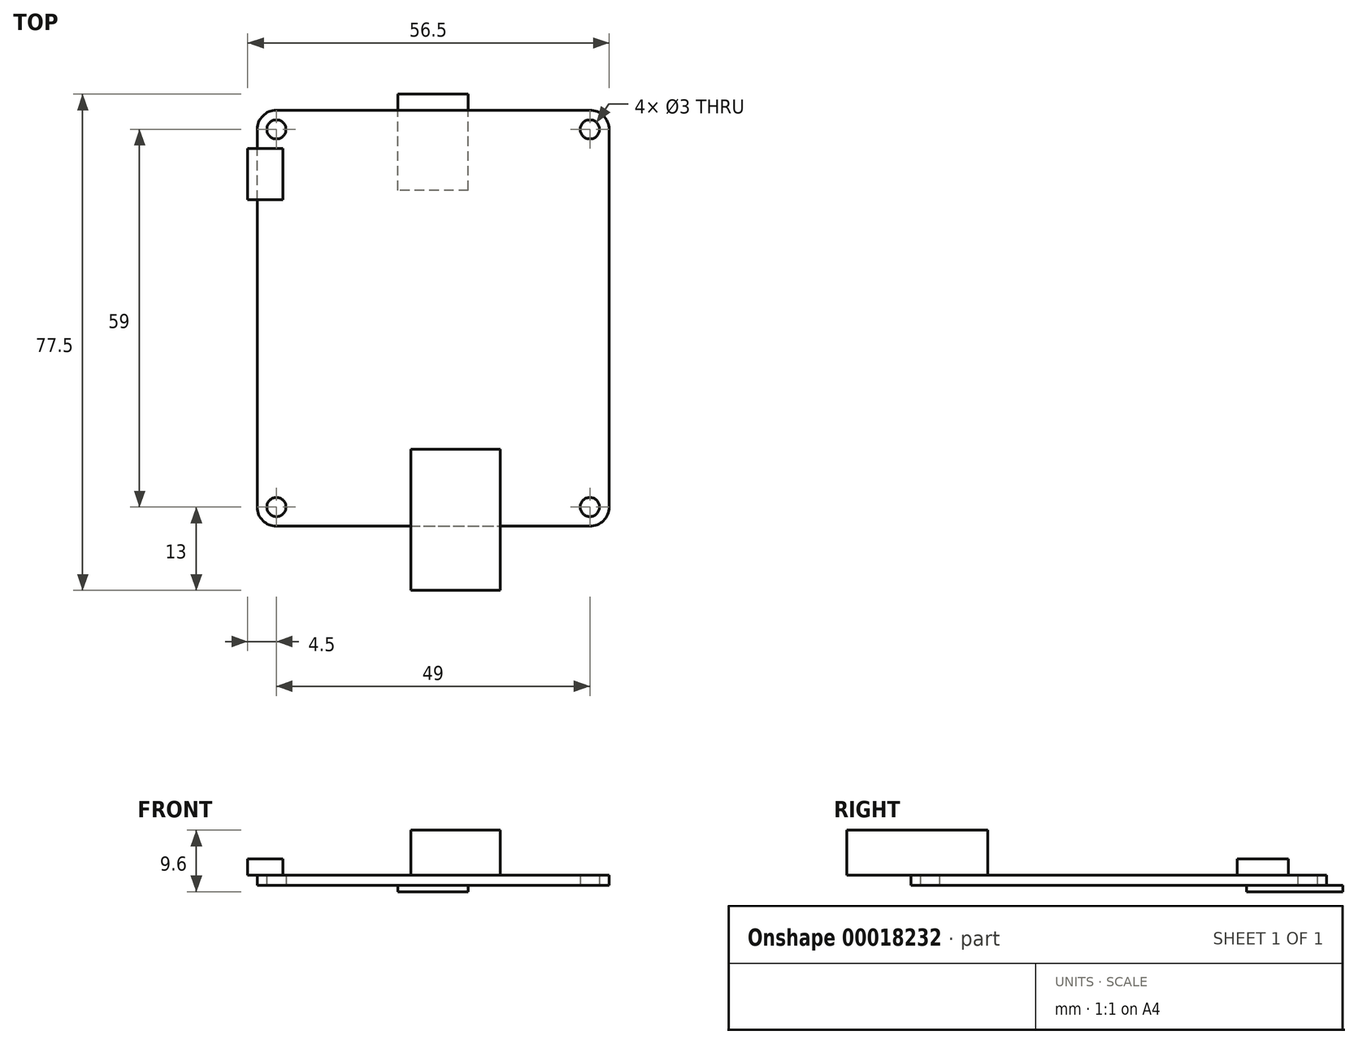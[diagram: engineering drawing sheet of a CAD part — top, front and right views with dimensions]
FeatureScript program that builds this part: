
annotation { "Feature Type Name" : "Feature", "Feature Type Description" : "" }
export const myFeature = defineFeature(function(context is Context, id is Id, definition is map)
    precondition{}
    {
        {
            var Q0;
            Q0=qCreatedBy(makeId("Top.planeOp"),FACE);
            var sketch = newSketch(context, id + "F0", { "sketchPlane" : qUnion([Q0])});
            skLineSegment(sketch, "E0.bottom", {"start": v(3, 0) * mm, "end": v(52, 0) * mm});
            skLineSegment(sketch, "E0.top", {"start": v(3, 65) * mm, "end": v(52, 65) * mm});
            skLineSegment(sketch, "E0.left", {"start": v(0, 3) * mm, "end": v(0, 62) * mm});
            skLineSegment(sketch, "E0.right", {"start": v(55, 3) * mm, "end": v(55, 62) * mm});
            skPoint(sketch, "E1.visualSharp", {"position": v(0, 0) * mm});
            skArc(sketch, "E1.filletArc", {"start": v(0, 3) * mm, "mid": v(0.88, 0.88) * mm, "end": v(3, 0) * mm});
            skPoint(sketch, "E2.visualSharp", {"position": v(0, 65) * mm});
            skArc(sketch, "E2.filletArc", {"start": v(3, 65) * mm, "mid": v(0.88, 64.12) * mm, "end": v(0, 62) * mm});
            skPoint(sketch, "E3.visualSharp", {"position": v(55, 65) * mm});
            skArc(sketch, "E3.filletArc", {"start": v(55, 62) * mm, "mid": v(54.12, 64.12) * mm, "end": v(52, 65) * mm});
            skPoint(sketch, "E4.visualSharp", {"position": v(55, 0) * mm});
            skArc(sketch, "E4.filletArc", {"start": v(52, 0) * mm, "mid": v(54.12, 0.88) * mm, "end": v(55, 3) * mm});
            skCircle(sketch, "E5", {"center": v(3, 3) * mm, "radius": 1.5 * mm});
            skCircle(sketch, "E6", {"center": v(52, 3) * mm, "radius": 1.5 * mm});
            skCircle(sketch, "E7", {"center": v(52, 62) * mm, "radius": 1.5 * mm});
            skCircle(sketch, "E8", {"center": v(3, 62) * mm, "radius": 1.5 * mm});
            skSolve(sketch);
        }
        {
            var Q0;
            Q0=makeQuery(id+"F0.imprint","IMPRINT",FACE,{"disambiguationData":[TD([[makeQuery(id+"F0.imprint","IMPRINT",EDGE,{"derivedFrom":sQuery(id+"F0.wireOp",EDGE,"E0.bottom")}),1.0]])]});
            extrude(context, id + "F1", {"entities" : qUnion([Q0]), "depth" : 1.6 * mm});
        }
        {
            var Q0;
            Q0=makeQuery(id+"F1.opExtrude","CAP_FACE",FACE,{"disambiguationData":[OSD([sQuery(id+"F0.wireOp",EDGE,"E0.bottom"),sQuery(id+"F0.wireOp",EDGE,"E0.top"),sQuery(id+"F0.wireOp",EDGE,"E0.left"),sQuery(id+"F0.wireOp",EDGE,"E0.right"),sQuery(id+"F0.wireOp",EDGE,"E1.filletArc"),sQuery(id+"F0.wireOp",EDGE,"E2.filletArc"),sQuery(id+"F0.wireOp",EDGE,"E3.filletArc"),sQuery(id+"F0.wireOp",EDGE,"E4.filletArc"),sQuery(id+"F0.wireOp",EDGE,"E5"),sQuery(id+"F0.wireOp",EDGE,"E6"),sQuery(id+"F0.wireOp",EDGE,"E7"),sQuery(id+"F0.wireOp",EDGE,"E8")])],"isStart":false});
            var sketch = newSketch(context, id + "F2", { "sketchPlane" : qUnion([Q0])});
            skLineSegment(sketch, "E9.bottom", {"start": v(24, 12) * mm, "end": v(38, 12) * mm});
            skLineSegment(sketch, "E9.top", {"start": v(24, -10) * mm, "end": v(38, -10) * mm});
            skLineSegment(sketch, "E9.left", {"start": v(24, 12) * mm, "end": v(24, -10) * mm});
            skLineSegment(sketch, "E9.right", {"start": v(38, 12) * mm, "end": v(38, -10) * mm});
            skLineSegment(sketch, "E10.bottom", {"start": v(4, 59) * mm, "end": v(-1.5, 59) * mm});
            skLineSegment(sketch, "E10.top", {"start": v(4, 51) * mm, "end": v(-1.5, 51) * mm});
            skLineSegment(sketch, "E10.left", {"start": v(4, 59) * mm, "end": v(4, 51) * mm});
            skLineSegment(sketch, "E10.right", {"start": v(-1.5, 59) * mm, "end": v(-1.5, 51) * mm});
            skSolve(sketch);
        }
        {
            var Q0;
            {var subQ3=sQuery(id+"F2.wireOp",EDGE,"E9.bottom");Q0=makeQuery(id+"F2.imprint","IMPRINT",FACE,{"disambiguationData":[TD([[makeQuery(id+"F2.imprint","IMPRINT",EDGE,{"derivedFrom":subQ3}),-1.0]])]});}
            var Q1;
            {var subQ5=sQuery(id+"F2.wireOp",EDGE,"E9.top");Q1=makeQuery(id+"F2.imprint","IMPRINT",FACE,{"disambiguationData":[TD([[makeQuery(id+"F2.imprint","IMPRINT",EDGE,{"derivedFrom":subQ5}),1.0]])]});}
            extrude(context, id + "F3", {"entities" : qUnion([Q0, Q1]), "operationType" : NewBodyOperationType.ADD, "depth" : 7 * mm});
        }
        {
            var Q0;
            {var subQ5=sQuery(id+"F2.wireOp",EDGE,"E10.left");Q0=makeQuery(id+"F2.imprint","IMPRINT",FACE,{"disambiguationData":[TD([[makeQuery(id+"F2.imprint","IMPRINT",EDGE,{"derivedFrom":subQ5}),-1.0]])]});}
            var Q1;
            {var subQ5=sQuery(id+"F2.wireOp",EDGE,"E10.right");Q1=makeQuery(id+"F2.imprint","IMPRINT",FACE,{"disambiguationData":[TD([[makeQuery(id+"F2.imprint","IMPRINT",EDGE,{"derivedFrom":subQ5}),1.0]])]});}
            extrude(context, id + "F4", {"entities" : qUnion([Q0, Q1]), "operationType" : NewBodyOperationType.ADD, "depth" : 2.5 * mm});
        }
        {
            var Q0;
            Q0=makeQuery(id+"F1.opExtrude","CAP_FACE",FACE,{"disambiguationData":[OSD([sQuery(id+"F0.wireOp",EDGE,"E0.bottom"),sQuery(id+"F0.wireOp",EDGE,"E0.top"),sQuery(id+"F0.wireOp",EDGE,"E0.left"),sQuery(id+"F0.wireOp",EDGE,"E0.right"),sQuery(id+"F0.wireOp",EDGE,"E1.filletArc"),sQuery(id+"F0.wireOp",EDGE,"E2.filletArc"),sQuery(id+"F0.wireOp",EDGE,"E3.filletArc"),sQuery(id+"F0.wireOp",EDGE,"E4.filletArc"),sQuery(id+"F0.wireOp",EDGE,"E5"),sQuery(id+"F0.wireOp",EDGE,"E6"),sQuery(id+"F0.wireOp",EDGE,"E7"),sQuery(id+"F0.wireOp",EDGE,"E8")])],"isStart":true});
            var sketch = newSketch(context, id + "F5", { "sketchPlane" : qUnion([Q0])});
            skLineSegment(sketch, "E11.bottom", {"start": v(33, -52.5) * mm, "end": v(22, -52.5) * mm});
            skLineSegment(sketch, "E11.top", {"start": v(33, -67.5) * mm, "end": v(22, -67.5) * mm});
            skLineSegment(sketch, "E11.left", {"start": v(33, -52.5) * mm, "end": v(33, -67.5) * mm});
            skLineSegment(sketch, "E11.right", {"start": v(22, -52.5) * mm, "end": v(22, -67.5) * mm});
            skSolve(sketch);
        }
        {
            var Q0;
            {var subQ5=sQuery(id+"F5.wireOp",EDGE,"E11.bottom");Q0=makeQuery(id+"F5.imprint","IMPRINT",FACE,{"disambiguationData":[TD([[makeQuery(id+"F5.imprint","IMPRINT",EDGE,{"derivedFrom":subQ5}),1.0]])]});}
            var Q1;
            {var subQ5=sQuery(id+"F5.wireOp",EDGE,"E11.top");Q1=makeQuery(id+"F5.imprint","IMPRINT",FACE,{"disambiguationData":[TD([[makeQuery(id+"F5.imprint","IMPRINT",EDGE,{"derivedFrom":subQ5}),-1.0]])]});}
            extrude(context, id + "F6", {"entities" : qUnion([Q0, Q1]), "operationType" : NewBodyOperationType.ADD, "depth" : 1 * mm});
        }
    });
